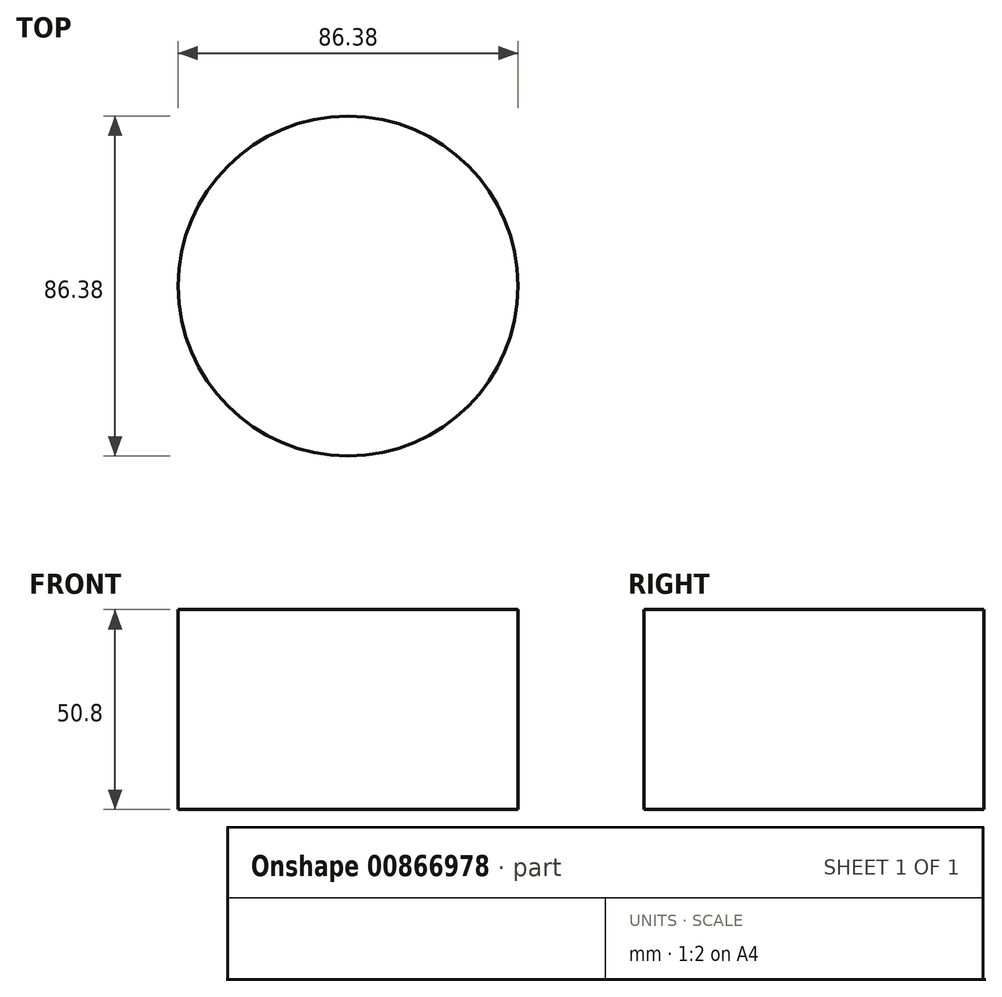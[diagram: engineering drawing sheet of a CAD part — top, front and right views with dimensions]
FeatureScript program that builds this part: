
annotation { "Feature Type Name" : "Feature", "Feature Type Description" : "" }
export const myFeature = defineFeature(function(context is Context, id is Id, definition is map)
    precondition{}
    {
        {
            var Q0;
            Q0=qCreatedBy(makeId("Top.planeOp"),FACE);
            var sketch = newSketch(context, id + "F0", { "sketchPlane" : qUnion([Q0])});
            skCircle(sketch, "E0", {"center": v(0, 0) * mm, "radius": 43.19 * mm});
            skSolve(sketch);
        }
        {
            var Q0;
            Q0=makeQuery(id+"F0.imprint","IMPRINT",FACE,{"disambiguationData":[TD([[makeQuery(id+"F0.imprint","IMPRINT",EDGE,{"derivedFrom":sQuery(id+"F0.wireOp",EDGE,"E0")}),1.0]])]});
            extrude(context, id + "F1", {"entities" : qUnion([Q0]), "depth" : 50.8 * mm, "offsetDistance" : 25.4 * mm});
        }
    });
